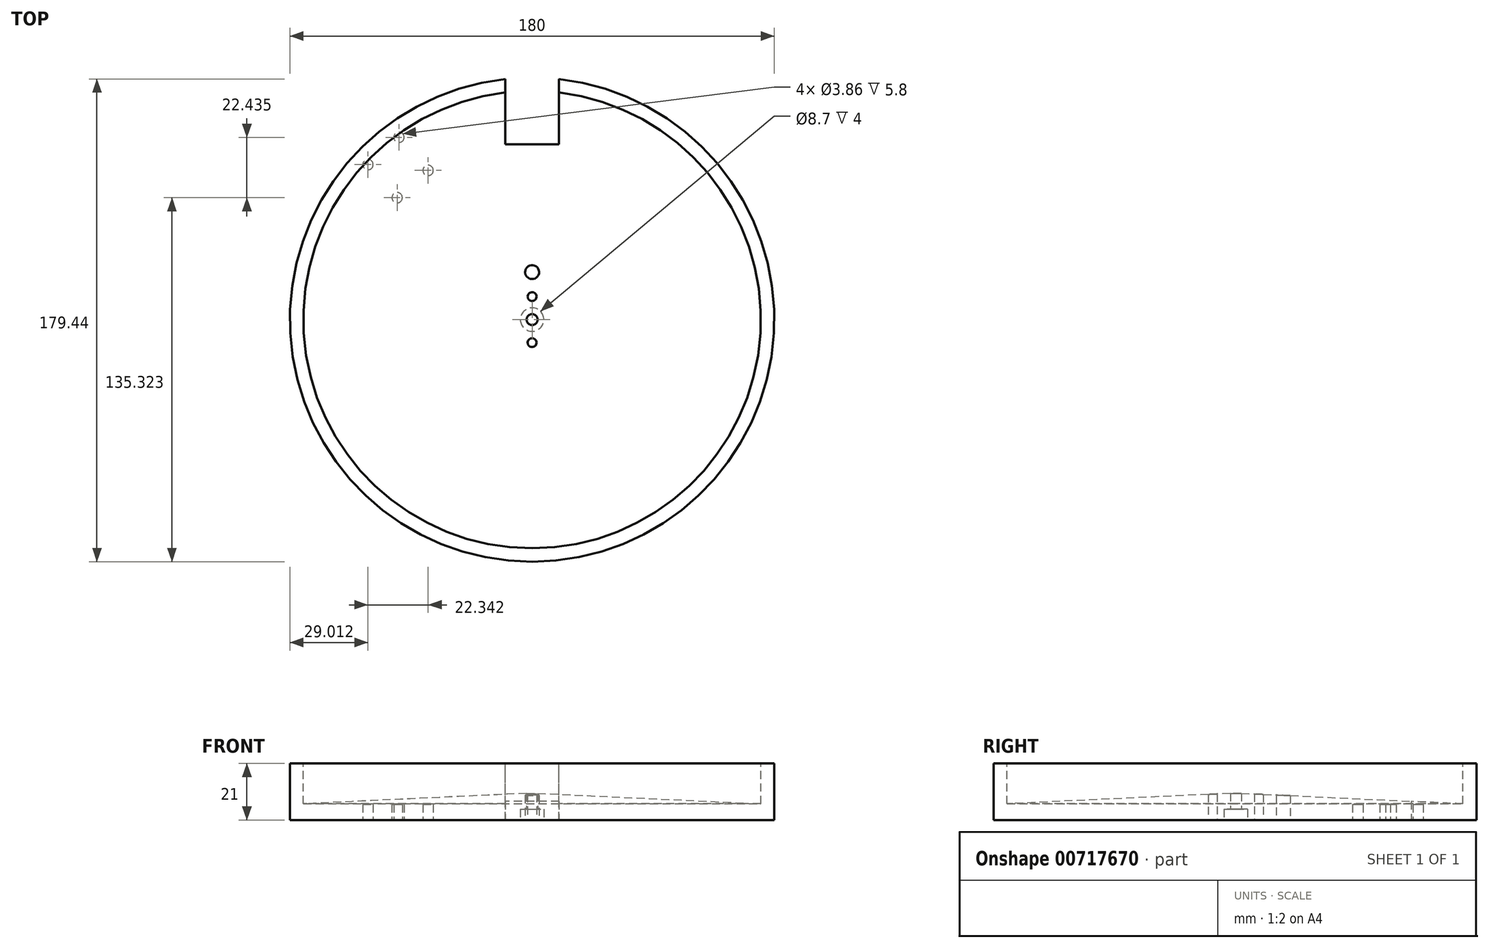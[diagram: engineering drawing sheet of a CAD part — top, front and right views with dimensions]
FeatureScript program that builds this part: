
annotation { "Feature Type Name" : "Feature", "Feature Type Description" : "" }
export const myFeature = defineFeature(function(context is Context, id is Id, definition is map)
    precondition{}
    {
        {
            var Q0;
            Q0=qCreatedBy(makeId("Front.planeOp"),FACE);
            var sketch = newSketch(context, id + "F0", { "sketchPlane" : qUnion([Q0])});
            skLineSegment(sketch, "E0", {"start": v(0, 0) * mm, "end": v(-90, 0) * mm});
            skLineSegment(sketch, "E1", {"start": v(-90, 0) * mm, "end": v(-90, 21) * mm});
            skLineSegment(sketch, "E2", {"start": v(-90, 21) * mm, "end": v(-85, 21) * mm});
            skLineSegment(sketch, "E3", {"start": v(-85, 21) * mm, "end": v(-85, 6) * mm});
            skLineSegment(sketch, "E4", {"start": v(-85, 6) * mm, "end": v(0, 10) * mm});
            skLineSegment(sketch, "E5", {"start": v(0, 10) * mm, "end": v(0, 0) * mm});
            skLineSegment(sketch, "E6", {"start": v(0, 43.42) * mm, "end": v(0, -67.66) * mm, "construction": true});
            skSolve(sketch);
        }
        {
            var Q0;
            Q0 = qSketchRegion(id + "F0", true);
            var Q1;
            Q1=sQuery(id+"F0.wireOp",EDGE,"E6");
            revolve(context, id + "F1", {"surfaceOperationType" : NewSurfaceOperationType.NEW, "entities" : qUnion([Q0]), "axis" : qUnion([Q1]), "revolveType" : RevolveType.FULL});
        }
        {
            var Q0;
            Q0=makeQuery(id+"F1.opRevolve","SWEPT_FACE",FACE,{"disambiguationData":[OSD([sQuery(id+"F0.wireOp",EDGE,"E0")])]});
            var sketch = newSketch(context, id + "F2", { "sketchPlane" : qUnion([Q0])});
            skCircle(sketch, "E7", {"center": v(0, 0) * mm, "radius": 2.05 * mm});
            skSolve(sketch);
        }
        {
            var Q0;
            Q0=qSketchRegion(id+"F2",true);
            extrude(context, id + "F3", {"entities" : qUnion([Q0]), "operationType" : NewBodyOperationType.REMOVE, "oppositeDirection" : true, "depth" : 20 * mm, "offsetDistance" : 25 * mm});
        }
        {
            var Q0;
            Q0=makeQuery(id+"F1.opRevolve","SWEPT_FACE",FACE,{"disambiguationData":[OSD([sQuery(id+"F0.wireOp",EDGE,"E0")])]});
            var sketch = newSketch(context, id + "F4", { "sketchPlane" : qUnion([Q0])});
            skLineSegment(sketch, "E8.bottom", {"start": v(10, -90.13) * mm, "end": v(-10, -90.13) * mm});
            skLineSegment(sketch, "E8.top", {"start": v(10, -65.13) * mm, "end": v(-10, -65.13) * mm});
            skLineSegment(sketch, "E8.left", {"start": v(10, -90.13) * mm, "end": v(10, -65.13) * mm});
            skLineSegment(sketch, "E8.right", {"start": v(-10, -90.13) * mm, "end": v(-10, -65.13) * mm});
            skPoint(sketch, "E8.middle", {"position": v(0, -77.63) * mm});
            skSolve(sketch);
        }
        {
            var Q0;
            Q0=qSketchRegion(id+"F4",true);
            extrude(context, id + "F5", {"entities" : qUnion([Q0]), "operationType" : NewBodyOperationType.REMOVE, "oppositeDirection" : true, "depth" : 25 * mm, "offsetDistance" : 25 * mm});
        }
        {
            var Q0;
            Q0=makeQuery(id+"F1.opRevolve","SWEPT_FACE",FACE,{"disambiguationData":[OSD([sQuery(id+"F0.wireOp",EDGE,"E0")])]});
            var sketch = newSketch(context, id + "F6", { "sketchPlane" : qUnion([Q0])});
            skLineSegment(sketch, "E9", {"start": v(-59.5, -67.53) * mm, "end": v(0, 0) * mm});
            skLineSegment(sketch, "E10", {"start": v(0, 0) * mm, "end": v(-59.5, -67.53) * mm, "construction": true});
            skLineSegment(sketch, "E11", {"start": v(-34.42, -69.85) * mm, "end": v(-67.76, -40.47) * mm, "construction": true});
            skCircle(sketch, "E12", {"center": v(-49.48, -67.76) * mm, "radius": 1.93 * mm});
            skPoint(sketch, "E12.first.point", {"position": v(-50.1, -69.59) * mm});
            skPoint(sketch, "E12.second.point", {"position": v(-48.16, -69.17) * mm});
            skPoint(sketch, "E12.third.point", {"position": v(-50.48, -66.1) * mm});
            skCircle(sketch, "E13", {"center": v(-50.16, -45.32) * mm, "radius": 1.93 * mm});
            skPoint(sketch, "E13.first.point", {"position": v(-51.6, -46.6) * mm});
            skPoint(sketch, "E13.second.point", {"position": v(-51.89, -44.47) * mm});
            skPoint(sketch, "E13.third.point", {"position": v(-48.33, -45.95) * mm});
            skCircle(sketch, "E14", {"center": v(-60.99, -57.62) * mm, "radius": 1.93 * mm});
            skPoint(sketch, "E14.first.point", {"position": v(-62.4, -58.93) * mm});
            skPoint(sketch, "E14.second.point", {"position": v(-62.34, -56.24) * mm});
            skPoint(sketch, "E14.third.point", {"position": v(-59.4, -56.53) * mm});
            skCircle(sketch, "E15", {"center": v(-38.65, -55.46) * mm, "radius": 1.93 * mm});
            skPoint(sketch, "E15.first.point", {"position": v(-39.9, -56.94) * mm});
            skPoint(sketch, "E15.second.point", {"position": v(-38.4, -57.38) * mm});
            skPoint(sketch, "E15.third.point", {"position": v(-38.56, -53.54) * mm});
            skSolve(sketch);
        }
        {
            var Q0;
            Q0=qSketchRegion(id+"F6",true);
            extrude(context, id + "F7", {"entities" : qUnion([Q0]), "operationType" : NewBodyOperationType.REMOVE, "oppositeDirection" : true, "depth" : 5.8 * mm, "offsetDistance" : 25 * mm});
        }
        {
            var Q0;
            Q0=makeQuery(id+"F1.opRevolve","SWEPT_FACE",FACE,{"disambiguationData":[OSD([sQuery(id+"F0.wireOp",EDGE,"E0")])]});
            var sketch = newSketch(context, id + "F8", { "sketchPlane" : qUnion([Q0])});
            skArc(sketch, "E16.0", {"start": v(10, -89.44) * mm, "mid": v(0, 90) * mm, "end": v(-10, -89.44) * mm});
            skCircle(sketch, "E17", {"center": v(0, -17.66) * mm, "radius": 2.6 * mm});
            skSolve(sketch);
        }
        {
            var Q0;
            Q0=qSketchRegion(id+"F8",true);
            extrude(context, id + "F9", {"entities" : qUnion([Q0]), "operationType" : NewBodyOperationType.REMOVE, "oppositeDirection" : true, "depth" : 25 * mm, "offsetDistance" : 25 * mm});
        }
        {
            var Q0;
            Q0=makeQuery(id+"F1.opRevolve","SWEPT_FACE",FACE,{"disambiguationData":[OSD([sQuery(id+"F0.wireOp",EDGE,"E0")])]});
            var sketch = newSketch(context, id + "F10", { "sketchPlane" : qUnion([Q0])});
            skCircle(sketch, "E18", {"center": v(0, 0) * mm, "radius": 4.35 * mm});
            skCircle(sketch, "E19", {"center": v(0, -8.56) * mm, "radius": 1.65 * mm});
            skCircle(sketch, "E20", {"center": v(0, 8.56) * mm, "radius": 1.65 * mm});
            skSolve(sketch);
        }
        {
            var Q0;
            Q0=qSketchRegion(id+"F10",true);
            extrude(context, id + "F11", {"entities" : qUnion([Q0]), "operationType" : NewBodyOperationType.REMOVE, "oppositeDirection" : true, "depth" : 4 * mm, "offsetDistance" : 25 * mm});
        }
        {
            var Q0;
            Q0=qCreatedBy(makeId("Front.planeOp"),FACE);
            var sketch = newSketch(context, id + "F12", { "sketchPlane" : qUnion([Q0])});
            skLineSegment(sketch, "E21", {"start": v(0, 120.79) * mm, "end": v(0, -107.96) * mm, "construction": true});
            skLineSegment(sketch, "E22", {"start": v(-111.44, 0) * mm, "end": v(110.44, 0) * mm, "construction": true});
            skSolve(sketch);
        }
        {
            var Q0;
            Q0=makeQuery(id+"F11.boolean.opBoolean","COPY",FACE,{"derivedFrom":makeQuery(id+"F11.opExtrude","CAP_FACE",FACE,{"disambiguationData":[OSD([sQuery(id+"F10.wireOp",EDGE,"E20")])],"isStart":false})});
            var Q1;
            Q1=makeQuery(id+"F11.boolean.opBoolean","COPY",FACE,{"derivedFrom":makeQuery(id+"F11.opExtrude","CAP_FACE",FACE,{"disambiguationData":[OSD([sQuery(id+"F10.wireOp",EDGE,"E19")])],"isStart":false})});
            extrude(context, id + "F13", {"entities" : qUnion([Q0, Q1]), "operationType" : NewBodyOperationType.REMOVE, "oppositeDirection" : true, "depth" : 25 * mm, "offsetDistance" : 25 * mm});
        }
        {
            var Q0;
            Q0=makeQuery(id+"F1.opRevolve","SWEPT_BODY",BODY,{"disambiguationData":[OSD([sQuery(id+"F0.wireOp",EDGE,"E0"),sQuery(id+"F0.wireOp",EDGE,"E1"),sQuery(id+"F0.wireOp",EDGE,"E2"),sQuery(id+"F0.wireOp",EDGE,"E3"),sQuery(id+"F0.wireOp",EDGE,"E4"),sQuery(id+"F0.wireOp",EDGE,"E5")])]});
            var Q1;
            Q1=sQuery(id+"F12.wireOp",EDGE,"E22");
            transform(context, id + "F14", {"entities" : qUnion([Q0]), "transformType" : TransformType.ROTATION, "transformAxis" : qUnion([Q1]), "angle" : 90 * degree, "oppositeDirection" : true, "makeCopy" : false});
        }
        {
            var Q0;
            Q0=makeQuery(id+"F1.opRevolve","SWEPT_BODY",BODY,{"disambiguationData":[OSD([sQuery(id+"F0.wireOp",EDGE,"E0"),sQuery(id+"F0.wireOp",EDGE,"E1"),sQuery(id+"F0.wireOp",EDGE,"E2"),sQuery(id+"F0.wireOp",EDGE,"E3"),sQuery(id+"F0.wireOp",EDGE,"E4"),sQuery(id+"F0.wireOp",EDGE,"E5")])]});
            var Q1;
            Q1=sQuery(id+"F0.wireOp",EDGE,"E6");
            var Q2;
            Q2=sQuery(id+"F12.wireOp",EDGE,"E22");
            transform(context, id + "F15", {"entities" : qUnion([Q0]), "transformType" : TransformType.ROTATION, "transformAxis" : qUnion([Q2]), "angle" : 270 * degree, "oppositeDirection" : true, "makeCopy" : false});
        }
    });
